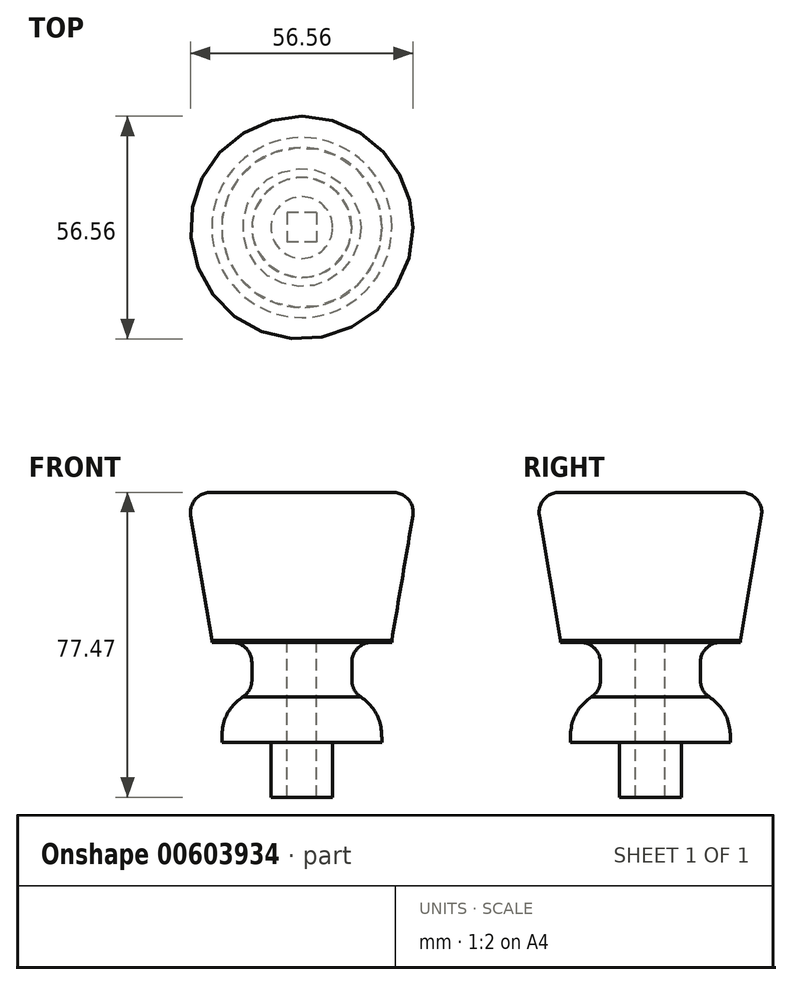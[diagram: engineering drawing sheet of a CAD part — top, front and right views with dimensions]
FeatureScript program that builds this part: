
annotation { "Feature Type Name" : "Feature", "Feature Type Description" : "" }
export const myFeature = defineFeature(function(context is Context, id is Id, definition is map)
    precondition{}
    {
        {
            var Q0;
            Q0=qCreatedBy(makeId("Top.planeOp"),FACE);
            var sketch = newSketch(context, id + "F0", { "sketchPlane" : qUnion([Q0])});
            skLineSegment(sketch, "E0.bottom", {"start": v(3.75, 3.75) * mm, "end": v(-3.75, 3.75) * mm});
            skLineSegment(sketch, "E0.top", {"start": v(3.75, -3.75) * mm, "end": v(-3.75, -3.75) * mm});
            skLineSegment(sketch, "E0.left", {"start": v(3.75, 3.75) * mm, "end": v(3.75, -3.75) * mm});
            skLineSegment(sketch, "E0.right", {"start": v(-3.75, 3.75) * mm, "end": v(-3.75, -3.75) * mm});
            skPoint(sketch, "E0.middle", {"position": v(0, 0) * mm});
            skCircle(sketch, "E1.0", {"center": v(0, 0) * mm, "radius": 7.84 * mm});
            skCircle(sketch, "E2", {"center": v(0, 0) * mm, "radius": 12.7 * mm});
            skCircle(sketch, "E3", {"center": v(0, 0) * mm, "radius": 20.32 * mm});
            skLineSegment(sketch, "E4.0", {"start": v(-33.12, 33.12) * mm, "end": v(-33.12, -33.12) * mm});
            skLineSegment(sketch, "E4.1", {"start": v(33.12, 33.12) * mm, "end": v(-33.12, 33.12) * mm});
            skLineSegment(sketch, "E4.2", {"start": v(33.12, 33.12) * mm, "end": v(33.12, -33.12) * mm});
            skLineSegment(sketch, "E4.3", {"start": v(33.12, -33.12) * mm, "end": v(-33.12, -33.12) * mm});
            skSolve(sketch);
        }
        {
            var Q0;
            Q0=makeQuery(id+"F0.imprint","IMPRINT",FACE,{"disambiguationData":[TD([[makeQuery(id+"F0.imprint","IMPRINT",EDGE,{"derivedFrom":sQuery(id+"F0.wireOp",EDGE,"E0.bottom")}),-1.0]])]});
            extrude(context, id + "F1", {"entities" : qUnion([Q0]), "depth" : -13.97 * mm, "offsetDistance" : 25.4 * mm});
        }
        {
            var Q0;
            Q0=makeQuery(id+"F0.imprint","IMPRINT",FACE,{"disambiguationData":[TD([[makeQuery(id+"F0.imprint","IMPRINT",EDGE,{"derivedFrom":sQuery(id+"F0.wireOp",EDGE,"E1.0")}),-1.0]])]});
            var Q1;
            Q1=makeQuery(id+"F0.imprint","IMPRINT",FACE,{"disambiguationData":[TD([[makeQuery(id+"F0.imprint","IMPRINT",EDGE,{"derivedFrom":sQuery(id+"F0.wireOp",EDGE,"E0.bottom")}),-1.0]])]});
            extrude(context, id + "F2", {"entities" : qUnion([Q0, Q1]), "operationType" : NewBodyOperationType.ADD, "depth" : 25.4 * mm, "offsetDistance" : 25.4 * mm});
        }
        {
            var Q0;
            Q0=makeQuery(id+"F0.imprint","IMPRINT",FACE,{"disambiguationData":[TD([[makeQuery(id+"F0.imprint","IMPRINT",EDGE,{"derivedFrom":sQuery(id+"F0.wireOp",EDGE,"E2")}),-1.0]])]});
            extrude(context, id + "F3", {"entities" : qUnion([Q0]), "operationType" : NewBodyOperationType.ADD, "depth" : 12.7 * mm, "offsetDistance" : 25.4 * mm});
        }
        {
            var Q0;
            Q0=makeQuery(id+"F2.opExtrude","CAP_FACE",FACE,{"disambiguationData":[OSD([sQuery(id+"F0.wireOp",EDGE,"E0.bottom"),sQuery(id+"F0.wireOp",EDGE,"E0.top"),sQuery(id+"F0.wireOp",EDGE,"E0.left"),sQuery(id+"F0.wireOp",EDGE,"E0.right"),sQuery(id+"F0.wireOp",EDGE,"E2")])],"isStart":false});
            var sketch = newSketch(context, id + "F4", { "sketchPlane" : qUnion([Q0])});
            skCircle(sketch, "E5", {"center": v(0, 0) * mm, "radius": 22.86 * mm});
            skSolve(sketch);
        }
        {
            var Q0;
            Q0=makeQuery(id+"F4.imprint","IMPRINT",FACE,{"disambiguationData":[TD([[makeQuery(id+"F4.imprint","IMPRINT",EDGE,{"derivedFrom":makeQuery(id+"F2.opExtrude","CAP_EDGE",EDGE,{"disambiguationData":[OSD([sQuery(id+"F0.wireOp",EDGE,"E0.bottom")])],"isStart":false})}),-1.0]])]});
            cPlane(context, id + "F5", {"entities" : qUnion([Q0]), "cplaneType" : CPlaneType.OFFSET, "offset" : 38.1 * mm, "width" : 152.4 * mm, "height" : 152.4 * mm});
        }
        {
            var Q0;
            Q0=qCreatedBy(id+"F5.planeOp",FACE);
            var sketch = newSketch(context, id + "F6", { "sketchPlane" : qUnion([Q0])});
            skCircle(sketch, "E6", {"center": v(0, 0) * mm, "radius": 29.21 * mm});
            skSolve(sketch);
        }
        {
            var Q0;
            Q0=makeQuery(id+"F4.imprint","IMPRINT",FACE,{"disambiguationData":[TD([[makeQuery(id+"F4.imprint","IMPRINT",EDGE,{"derivedFrom":sQuery(id+"F4.wireOp",EDGE,"E5")}),1.0]])]});
            var Q1;
            Q1=makeQuery(id+"F4.imprint","IMPRINT",FACE,{"disambiguationData":[TD([[makeQuery(id+"F4.imprint","IMPRINT",EDGE,{"derivedFrom":makeQuery(id+"F2.opExtrude","CAP_EDGE",EDGE,{"disambiguationData":[OSD([sQuery(id+"F0.wireOp",EDGE,"E0.bottom")])],"isStart":false})}),-1.0]])]});
            var Q2;
            Q2=makeQuery(id+"F4.imprint","IMPRINT",FACE,{"disambiguationData":[TD([[makeQuery(id+"F4.imprint","IMPRINT",EDGE,{"derivedFrom":makeQuery(id+"F2.opExtrude","CAP_EDGE",EDGE,{"disambiguationData":[OSD([sQuery(id+"F0.wireOp",EDGE,"E0.bottom")])],"isStart":false})}),1.0]])]});
            extrude(context, id + "F7", {"entities" : qUnion([Q0, Q1, Q2]), "operationType" : NewBodyOperationType.ADD, "depth" : 0.5 * mm, "offsetDistance" : 25.4 * mm});
        }
        {
            var Q1;
            Q1=makeQuery(id+"F7.opExtrude","CAP_FACE",FACE,{"disambiguationData":[OSD([sQuery(id+"F4.wireOp",EDGE,"E5")])],"isStart":false});
            var Q2;
            Q2=makeQuery(id+"F6.imprint","IMPRINT",FACE,{"disambiguationData":[TD([[makeQuery(id+"F6.imprint","IMPRINT",EDGE,{"derivedFrom":sQuery(id+"F6.wireOp",EDGE,"E6")}),1.0]])]});
            loft(context, id + "F8", {"operationType" : NewBodyOperationType.ADD, "sheetProfilesArray" : [{ "sheetProfileEntities" : qUnion([Q1]) }, { "sheetProfileEntities" : qUnion([Q2]) }]});
        }
        {
            var Q0;
            Q0=makeQuery(id+"F8.opLoft","MID_CAP_EDGE",EDGE,{"disambiguationData":[OSD([sQuery(id+"F4.wireOp",EDGE,"E5"),sQuery(id+"F6.wireOp",EDGE,"E6")])],"capPos":1.0});
            fillet(context, id + "F9", {"entities" : qUnion([Q0]), "radius" : 5.08 * mm, "tangentPropagation" : true, "allowEdgeOverflow" : false});
        }
        {
            var Q0;
            Q0=makeQuery(id+"F3.opExtrude","CAP_EDGE",EDGE,{"disambiguationData":[OSD([sQuery(id+"F0.wireOp",EDGE,"E3")])],"isStart":false});
            fillet(context, id + "F10", {"entities" : qUnion([Q0]), "radius" : 12.7 * mm, "tangentPropagation" : true, "rho" : .5, "crossSection" : FilletCrossSection.CONIC, "allowEdgeOverflow" : false});
        }
        {
            var Q0;
            Q0=makeQuery(id+"F2.opExtrude","CAP_EDGE",EDGE,{"disambiguationData":[OSD([sQuery(id+"F0.wireOp",EDGE,"E2")])],"isStart":false});
            var Q1;
            Q1=makeQuery(id+"F10.opFillet","BLEND_EDGE",EDGE,{"blendedFrom":[makeQuery(id+"F3.opExtrude","CAP_EDGE",EDGE,{"disambiguationData":[OSD([sQuery(id+"F0.wireOp",EDGE,"E3")])],"isStart":false}),makeQuery(id+"F2.opExtrude","SWEPT_FACE",FACE,{"disambiguationData":[OSD([sQuery(id+"F0.wireOp",EDGE,"E2")])]})],"blendedInto":[makeQuery(id+"F2.opExtrude","SWEPT_FACE",FACE,{"disambiguationData":[OSD([sQuery(id+"F0.wireOp",EDGE,"E2")])]})]});
            fillet(context, id + "F11", {"entities" : qUnion([Q0, Q1]), "radius" : 5.08 * mm, "tangentPropagation" : true, "allowEdgeOverflow" : false});
        }
    });
